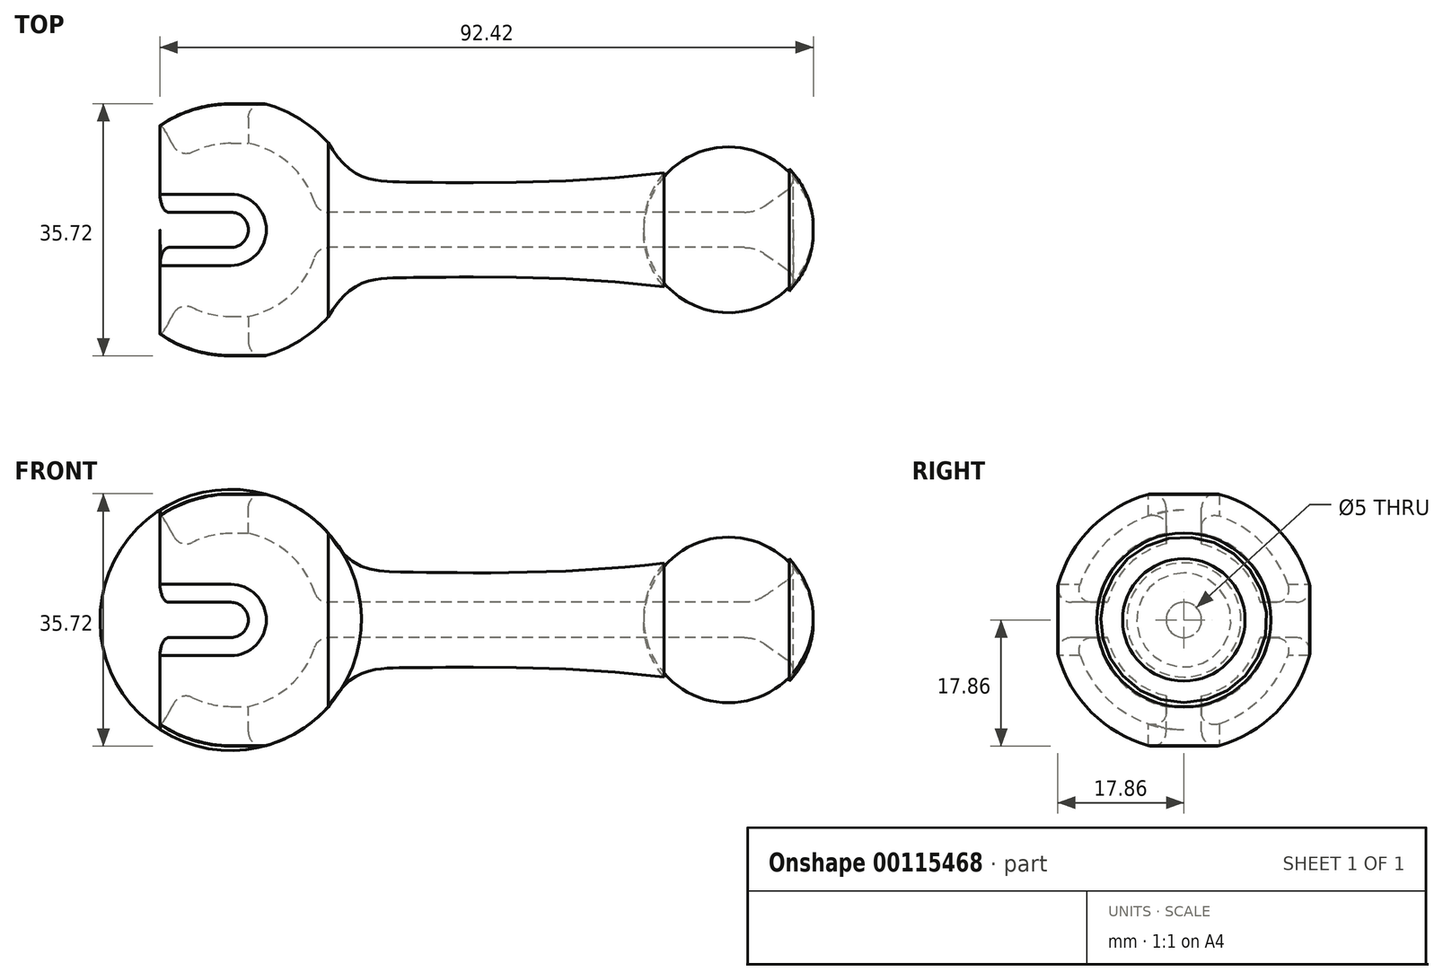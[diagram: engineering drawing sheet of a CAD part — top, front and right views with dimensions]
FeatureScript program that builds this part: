
annotation { "Feature Type Name" : "Feature", "Feature Type Description" : "" }
export const myFeature = defineFeature(function(context is Context, id is Id, definition is map)
    precondition{}
    {
        {
            var Q0;
            Q0=qCreatedBy(makeId("Front.planeOp"),FACE);
            var sketch = newSketch(context, id + "F0", { "sketchPlane" : qUnion([Q0])});
            skLineSegment(sketch, "E0", {"start": v(12.5, 0) * mm, "end": v(57.5, 0) * mm});
            skArc(sketch, "E1", {"start": v(12.25, 2.5) * mm, "mid": v(4.69, 11.59) * mm, "end": v(-7.07, 10.3) * mm});
            skFitSpline(sketch, "E2", {"points": [v(13.78, 12.32) * mm, v(24.8, 6.77) * mm, v(61.3, 8.08) * mm], "startDerivative": vector(27.08, -44.66) * mm, "endDerivative": vector(62.99, 8.12) * mm});
            skLineSegment(sketch, "E3", {"start": v(12.25, 2.5) * mm, "end": v(74.25, 2.5) * mm});
            skLineSegment(sketch, "E4", {"start": v(74.25, 2.5) * mm, "end": v(80.46, 6.85) * mm});
            skArc(sketch, "E5.trimOffspring", {"start": v(80.46, 6.85) * mm, "mid": v(71.19, 12.25) * mm, "end": v(61.3, 8.08) * mm});
            skPoint(sketch, "E6.end.orphan", {"position": v(82.25, 2.5) * mm});
            skPoint(sketch, "E7.orphan", {"position": v(82.5, 0) * mm});
            skArc(sketch, "E8", {"start": v(13.78, 12.32) * mm, "mid": v(2.48, 18.32) * mm, "end": v(-10, 15.54) * mm});
            skLineSegment(sketch, "E9", {"start": v(-7.07, 10.3) * mm, "end": v(-10, 15.54) * mm});
            skSolve(sketch);
        }
        {
            var Q0;
            Q0=makeQuery(id+"F0.imprint","IMPRINT",FACE,{"disambiguationData":[TD([[makeQuery(id+"F0.imprint","IMPRINT",EDGE,{"derivedFrom":sQuery(id+"F0.wireOp",EDGE,"E1")}),-1.0]])]});
            var Q1;
            Q1=sQuery(id+"F0.wireOp",EDGE,"E0");
            revolve(context, id + "F1", {"entities" : qUnion([Q0]), "axis" : qUnion([Q1]), "revolveType" : RevolveType.FULL});
        }
        {
            var Q0;
            Q0=makeQuery(id+"F1.opRevolve","SWEPT_EDGE",EDGE,{"disambiguationData":[OSD([sQuery(id+"F0.wireOp",EDGE,"E1"),sQuery(id+"F0.wireOp",EDGE,"CbFEBDJi-CplH-pibZ-NPAv-z09MQRNn6UNR")])]});
            var Q1;
            Q1=makeQuery(id+"F1.opRevolve","SWEPT_EDGE",EDGE,{"disambiguationData":[OSD([sQuery(id+"F0.wireOp",EDGE,"E4"),sQuery(id+"F0.wireOp",EDGE,"E5.trimOffspring")])]});
            fillet(context, id + "F2", {"entities" : qUnion([Q0, Q1]), "radius" : 2 * mm, "tangentPropagation" : true, "allowEdgeOverflow" : false});
        }
        {
            var Q0;
            Q0=makeQuery(id+"F1.opRevolve","SWEPT_EDGE",EDGE,{"disambiguationData":[OSD([sQuery(id+"F0.wireOp",EDGE,"E3"),sQuery(id+"F0.wireOp",EDGE,"E4")])]});
            fillet(context, id + "F3", {"entities" : qUnion([Q0]), "radius" : 5 * mm, "tangentPropagation" : true, "allowEdgeOverflow" : false});
        }
        {
            var Q0;
            Q0=qCreatedBy(makeId("Front.planeOp"),FACE);
            var sketch = newSketch(context, id + "F4", { "sketchPlane" : qUnion([Q0])});
            skArc(sketch, "E10", {"start": v(0, -2.5) * mm, "mid": v(2.5, 0) * mm, "end": v(0, 2.5) * mm});
            skLineSegment(sketch, "E11", {"start": v(0, 2.5) * mm, "end": v(-10.01, 2.5) * mm});
            skLineSegment(sketch, "E12", {"start": v(0, -2.5) * mm, "end": v(-10.01, -2.5) * mm});
            skLineSegment(sketch, "E13", {"start": v(-10.01, -2.5) * mm, "end": v(-10.01, 2.5) * mm});
            skSolve(sketch);
        }
        {
            var Q0;
            Q0 = qSketchRegion(id + "F4", true);
            extrude(context, id + "F5", {"entities" : qUnion([Q0]), "operationType" : NewBodyOperationType.REMOVE, "endBound" : BoundingType.SYMMETRIC, "oppositeDirection" : true, "depth" : 50 * mm});
        }
        {
            var Q0;
            Q0=qCreatedBy(makeId("Top.planeOp"),FACE);
            var sketch = newSketch(context, id + "F6", { "sketchPlane" : qUnion([Q0])});
            skArc(sketch, "E14", {"start": v(0, -2.5) * mm, "mid": v(2.5, 0) * mm, "end": v(0, 2.5) * mm});
            skLineSegment(sketch, "E15", {"start": v(0, 2.5) * mm, "end": v(-10.04, 2.5) * mm});
            skLineSegment(sketch, "E16", {"start": v(0, -2.5) * mm, "end": v(-9.97, -2.5) * mm});
            skLineSegment(sketch, "E17", {"start": v(-9.97, -2.5) * mm, "end": v(-10.04, 2.5) * mm});
            skSolve(sketch);
        }
        {
            var Q0;
            Q0 = qSketchRegion(id + "F6", true);
            extrude(context, id + "F7", {"entities" : qUnion([Q0]), "operationType" : NewBodyOperationType.REMOVE, "endBound" : BoundingType.SYMMETRIC, "oppositeDirection" : true, "depth" : 50 * mm});
        }
        {
            var Q0;
            Q0=makeQuery(id+"F5.boolean.opBoolean","INTERSECT",EDGE,{"disambiguationData":[OD(1.0)],"derivedFrom":[makeQuery(id+"F1.opRevolve","SWEPT_FACE",FACE,{"disambiguationData":[OSD([sQuery(id+"F0.wireOp",EDGE,"E8")])]}),makeQuery(id+"F5.opExtrude","SWEPT_FACE",FACE,{"disambiguationData":[OSD([sQuery(id+"F4.wireOp",EDGE,"E10")])]})]});
            var Q1;
            Q1=makeQuery(id+"F7.boolean.opBoolean","INTERSECT",EDGE,{"disambiguationData":[OD(1.0)],"derivedFrom":[makeQuery(id+"F1.opRevolve","SWEPT_FACE",FACE,{"disambiguationData":[OSD([sQuery(id+"F0.wireOp",EDGE,"E8")])]}),makeQuery(id+"F7.opExtrude","SWEPT_FACE",FACE,{"disambiguationData":[OSD([sQuery(id+"F6.wireOp",EDGE,"E14")])]})]});
            var Q2;
            Q2=makeQuery(id+"F5.boolean.opBoolean","INTERSECT",EDGE,{"disambiguationData":[OD(0.0)],"derivedFrom":[makeQuery(id+"F1.opRevolve","SWEPT_FACE",FACE,{"disambiguationData":[OSD([sQuery(id+"F0.wireOp",EDGE,"E8")])]}),makeQuery(id+"F5.opExtrude","SWEPT_FACE",FACE,{"disambiguationData":[OSD([sQuery(id+"F4.wireOp",EDGE,"E10")])]})]});
            var Q3;
            Q3=makeQuery(id+"F7.boolean.opBoolean","INTERSECT",EDGE,{"disambiguationData":[OD(0.0)],"derivedFrom":[makeQuery(id+"F1.opRevolve","SWEPT_FACE",FACE,{"disambiguationData":[OSD([sQuery(id+"F0.wireOp",EDGE,"E8")])]}),makeQuery(id+"F7.opExtrude","SWEPT_FACE",FACE,{"disambiguationData":[OSD([sQuery(id+"F6.wireOp",EDGE,"E14")])]})]});
            fillet(context, id + "F8", {"entities" : qUnion([Q0, Q1, Q2, Q3]), "radius" : 2 * mm, "tangentPropagation" : true, "allowEdgeOverflow" : false});
        }
    });
